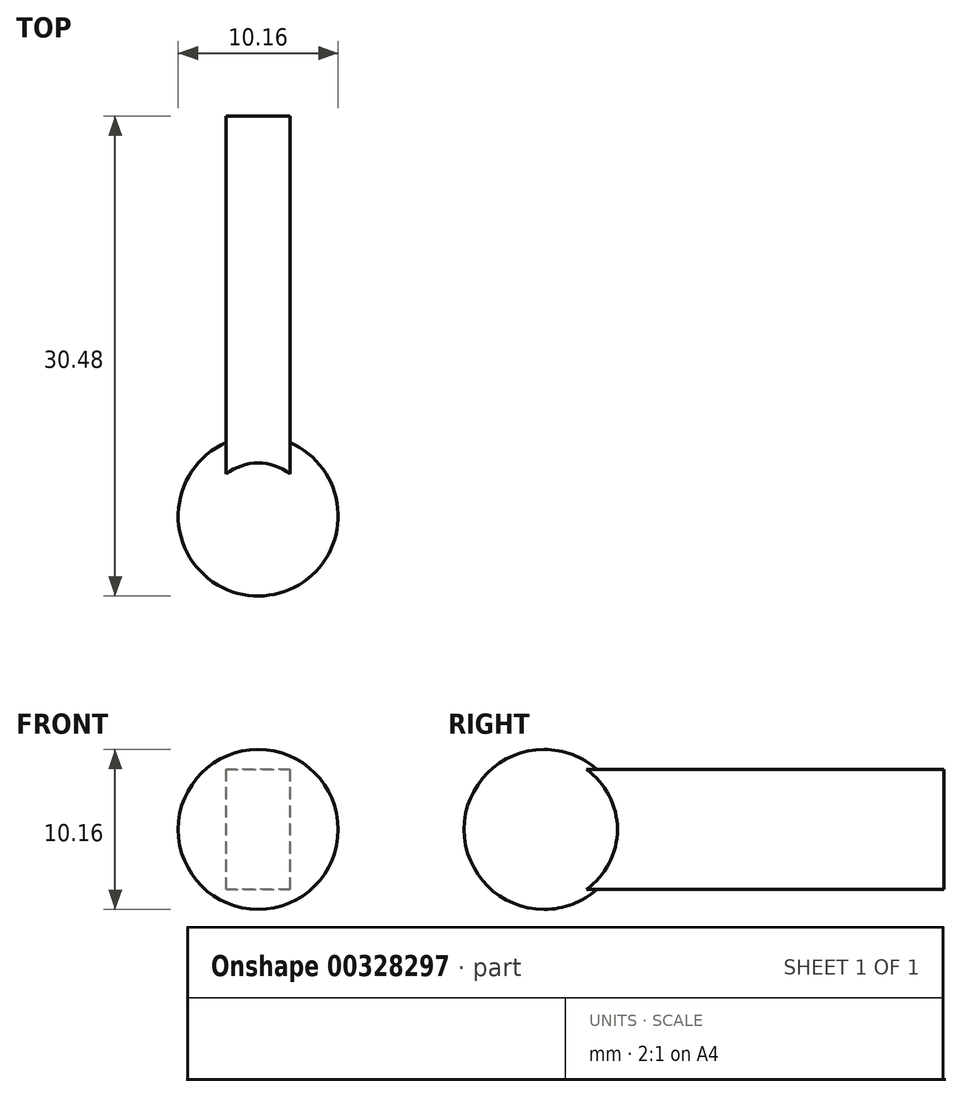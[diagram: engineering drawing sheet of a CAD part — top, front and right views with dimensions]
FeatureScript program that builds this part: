
annotation { "Feature Type Name" : "Feature", "Feature Type Description" : "" }
export const myFeature = defineFeature(function(context is Context, id is Id, definition is map)
    precondition{}
    {
        {
            var Q0;
            Q0=qCreatedBy(makeId("Front.planeOp"),FACE);
            var sketch = newSketch(context, id + "F0", { "sketchPlane" : qUnion([Q0])});
            skLineSegment(sketch, "E0.bottom", {"start": v(-2.03, 3.81) * mm, "end": v(2.03, 3.81) * mm});
            skLineSegment(sketch, "E0.top", {"start": v(-2.03, -3.81) * mm, "end": v(2.03, -3.81) * mm});
            skLineSegment(sketch, "E0.left", {"start": v(-2.03, 3.81) * mm, "end": v(-2.03, -3.81) * mm});
            skLineSegment(sketch, "E0.right", {"start": v(2.03, 3.81) * mm, "end": v(2.03, -3.81) * mm});
            skSolve(sketch);
        }
        {
            var Q0;
            Q0 = qSketchRegion(id + "F0", true);
            extrude(context, id + "F1", {"entities" : qUnion([Q0]), "depth" : 25.4 * mm});
        }
        {
            var Q0;
            Q0=makeQuery(id+"F1.opExtrude","CAP_FACE",FACE,{"disambiguationData":[OSD([sQuery(id+"F0.wireOp",EDGE,"E0.bottom"),sQuery(id+"F0.wireOp",EDGE,"E0.top"),sQuery(id+"F0.wireOp",EDGE,"E0.left"),sQuery(id+"F0.wireOp",EDGE,"E0.right")])],"isStart":false});
            var sketch = newSketch(context, id + "F2", { "sketchPlane" : qUnion([Q0])});
            skArc(sketch, "E1", {"start": v(0, 5.08) * mm, "mid": v(-5.08, 0) * mm, "end": v(0, -5.08) * mm});
            skLineSegment(sketch, "E2", {"start": v(0, 5.08) * mm, "end": v(0, -5.08) * mm});
            skSolve(sketch);
        }
        {
            var Q0;
            Q0 = qSketchRegion(id + "F2", true);
            var Q1;
            Q1=sQuery(id+"F2.wireOp",EDGE,"E2");
            revolve(context, id + "F3", {"operationType" : NewBodyOperationType.ADD, "entities" : qUnion([Q0]), "axis" : qUnion([Q1]), "revolveType" : RevolveType.FULL});
        }
    });
